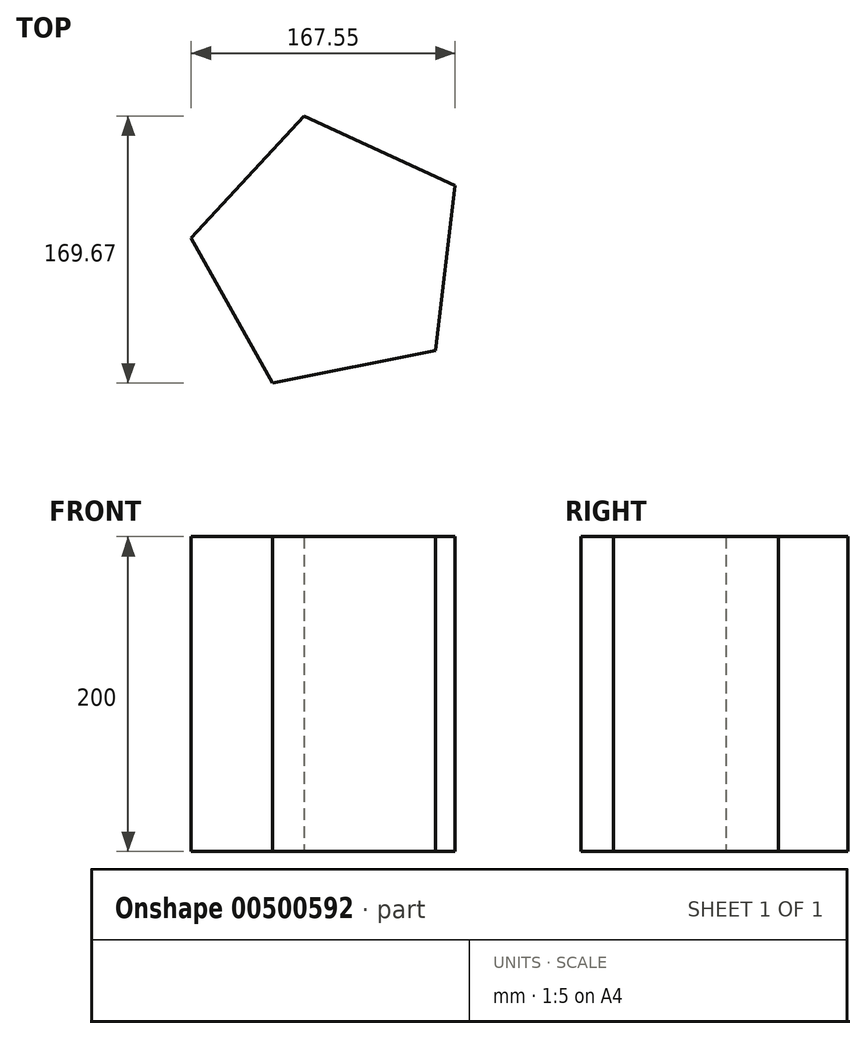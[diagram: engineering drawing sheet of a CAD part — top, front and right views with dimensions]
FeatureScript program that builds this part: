
annotation { "Feature Type Name" : "Feature", "Feature Type Description" : "" }
export const myFeature = defineFeature(function(context is Context, id is Id, definition is map)
    precondition{}
    {
        {
            var Q0;
            Q0=qCreatedBy(makeId("Top.planeOp"),FACE);
            var sketch = newSketch(context, id + "F0", { "sketchPlane" : qUnion([Q0])});
            skCircle(sketch, "E0.cCircle", {"center": v(0, 0) * mm, "radius": 89.82 * mm, "construction": true});
            skLineSegment(sketch, "E0.0", {"start": v(65.98, -60.95) * mm, "end": v(-37.58, -81.58) * mm});
            skLineSegment(sketch, "E0.1", {"start": v(-37.58, -81.58) * mm, "end": v(-89.2, 10.53) * mm});
            skLineSegment(sketch, "E0.2", {"start": v(-89.2, 10.53) * mm, "end": v(-17.55, 88.09) * mm});
            skLineSegment(sketch, "E0.3", {"start": v(-17.55, 88.09) * mm, "end": v(78.35, 43.91) * mm});
            skLineSegment(sketch, "E0.4", {"start": v(78.35, 43.91) * mm, "end": v(65.98, -60.95) * mm});
            skSolve(sketch);
        }
        {
            var Q0;
            Q0=makeQuery(id+"F0.imprint","IMPRINT",FACE,{"disambiguationData":[TD([[makeQuery(id+"F0.imprint","IMPRINT",EDGE,{"derivedFrom":sQuery(id+"F0.wireOp",EDGE,"E0.0")}),-1.0]])]});
            extrude(context, id + "F1", {"entities" : qUnion([Q0]), "depth" : 200 * mm});
        }
    });
